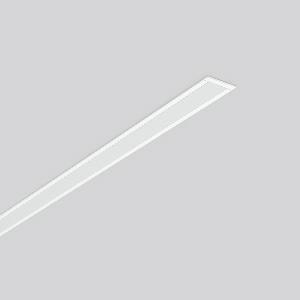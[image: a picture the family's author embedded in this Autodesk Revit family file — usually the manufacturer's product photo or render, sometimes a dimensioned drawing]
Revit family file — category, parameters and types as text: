
# Revit family: less_is_more_27_312176_002_1_965f
name_source: partatom
category: Lighting Fixtures
units: mm (PartAtom-declared; Revit-internal decimal feet)

## family parameters
Cut with Voids When Loaded = No
Host = Face
Light Source = No
Part Type = Normal
Room Calculation Point = No
Round Connector Dimension = Use Diameter
Shared = No

## types (1)
- LESS IS MORE 27 (1 x LED Modul 840, 1950 lm, 4000)
    Apparent Load = 25 VA
    CIE Flux Codes = 48 79 96 100 100
    Color Rendering = 80
    Color Temperature = 4000
    Default Elevation = 1800 mm
    Description = Series: LESS IS MORE 27
Recessed ceiling and wall luminaire with slim design. Housing: extruded aluminium profile, powder-coated. End cap aluminium powder-coated. Diffuser made of non-yellowing plastic (PMMA), opal. Suitable for Recessed ceiling mounting, wall (recessed). External driver with connecting cable. 
Colour: traffic white, matt (RAL 9016)
Length: 1014 mm
Width: 38 mm
Height: 2 mm
Cut-out length: 1006 mm
Cut-out width: 30 mm
Recess height: 45-60 mm
Luminaire: recess height: 37 mm
Lamp: LED
Socket: without socket
Colour temperature: 4000K
Colour rendering index (CRI): 82
System power: 25 W
Rated luminous flux: 1950 lm
Luminous efficiency: 78 lm/W
Control gear: Regulated power supply
Protection class: II
Type of protection: IP 20
    Height = 0 mm  [stored 0 ft]
    Lamp = 1 x LED Modul 840
    Lamp Light Flux = 1950 lm
    Lamp count = 1
    Length = 1014 mm
    Lifetime = 50000 h
    Luminous efficacy = 78 lm/W
    Manufacturer = RZB
    ModVariant = No
    Model = 312176.002.1
    Mounting Place = Ceiling, Wall
    Mounting Type = Recessed
    Number of Poles = 1
    OnlyDefault = Yes
    Power Factor = 1
    Product Name = LESS IS MORE 27
    Product group = Recessed LED linear luminaires
    ProductGroupID = 407
    Protection Class = Protection class II
    Protection Degree = IP 20
    RLX_Detail_Level = 1
    RLX_Emergency_Light_Flux = 0 lm
    RLX_Emergency_Type = 0
    RLX_Emergency_Type_DB = No
    RlxData = <blob elided: 21557 chars, md5=708d34ee>
    Socket = socket
    Standby Power = 0 W
    System Light Flux = 1950 lm
    System Power = 25 W
    Type Comments = Product without accessories
    Type Image = 312176.002.jpg
    URL = http://relux.com
    VarID = ---
    Voltage = 230 V
    Voltage Range = 220-240 V
    Weight = 0.00 kg
    Width = 38 mm

note: [stored X ft] marks values corroborated as IEEE doubles in the binary element streams (Revit-internal decimal feet)

## geometry (parser evidence)
native form markers: Blend x4, Sweep x11
no freeform markers — native parametric forms only
